# Revit family: QF_BPRO_CE 66-54_574906
name_source: partatom
category: Sonderausstattung
revit_build: Autodesk Revit 2018 (Build: 20190510_1515(x64)
units: mm (PartAtom-declared; Revit-internal decimal feet)

## family parameters
Arbeitsebenenbasiert = Nein
Beim Laden mit Abzugskörper schneiden = Nein
Bemaßung runder Anschluss = Durchmesser verwenden
Gemeinsam genutzt = Nein
Immer vertikal = Ja
Raumberechnungspunkt = Ja
Teiletyp = Normal

## types (1)
- CE 66-54
    Abdeckhaube Höhe = 167 mm  [stored 0.5479 ft]
    Abdeckhaube Länge = 710 mm
    Abdeckhaube Tiefe = 590 mm  [stored 1.9357 ft]
    Artikel Nummer = 574906
    Beschreibung = Korbspender, geschlossene Ausführung;
Korbmaße 650 x 530 mm;
Kapazität 6 Körbe à 115 mm oder 9 Körbe à 75 mm
    Beschreibung durch Hersteller analog Leistungsverzeichniskurztext = Abmessungen

Länge:					  885 mm
Breite:					  700 mm
Höhe:					  911 mm
Höhe (mit Option Abdeckhaube):		1067 mm
Arbeitshöhe:					  900 mm


Ausführung

Aufbau
Der Korbspender besteht komplett aus CNS 18/10. Die Oberfläche ist mikroliert. 
Der Korpus ist einwandig und kompakt in geschlossener Ausführung aufgebaut. Dadurch sind die Körbe vor Verschmutzung geschützt. 
Die Körbe werden auf eine Plattform aufgesetzt. Der Aufbau des Gerätes schützt vor dem Verrutschen der Körbe innerhalb des Spenders.
Durch Ein- bzw. Aushängen der Zugfedern kann die Federspannung entsprechend dem Stapelgut reguliert werden, um eine gleichbleibende Ausgabehöhe zu gewährleisten.
Bedienseitig ist ein CNS-Sicherheits-Schiebegriff mit seitlichen Stoßschutzelementen aus Kunststoff (Polyamid) angebracht.
Fahrbar ist der Spender mittels rostfreien Kunststoffrollen (4 Lenkrollen, 2 davon mit Feststeller mit 125 mm ø). Massive Stoßecken aus Kunststoff (Polyamid) an allen vier Ecken schützen vor Beschädigung.


Zubehör/ Optionen

•	Körbe aus Stahldraht, Kunststoff beschichtet
650 x 530 x 75 mm oder 650 x 530 x 115 mm
•	Körbe aus Edelstahl, rostfrei
650 x 530 x 75 mm oder 650 x 530 x 115 mm
•	Abdeckhaube (710 x 590 mm), Polycarbonat
Stapelhöhe mit Abdeckhaube:	680 mm
Stapelhöhe ohne Abdeckhaube:	540 mm
•	Weitere Zubehöre und Rollenausführungen siehe Gesamt-Preisliste



Technische Daten

Werkstoff:		CNS 18/10
Gewicht:		48 kg 
Plattform:		660 x 540 mm
Kapazität:		6 Körbe mit Höhe 115 mm,
		9 Körbe mit Höhe 75 mm


Besonderheit

•	Veränderung der Federspannung möglich
•	gemäß DIN 18665, Teil 6


Fabrikat

Hersteller:			B.PRO
Modell:				CE 66/ 54
Best.Nr.			574 906
    Beschreibung durch Hersteller analog Leistungsverzeichnislangtext = Abmessungen

Länge:					  885 mm
Breite:					  700 mm
Höhe:					  911 mm
Höhe (mit Option Abdeckhaube):		1067 mm
Arbeitshöhe:					  900 mm


Ausführung

Aufbau
Der Korbspender besteht komplett aus CNS 18/10. Die Oberfläche ist mikroliert. 
Der Korpus ist einwandig und kompakt in geschlossener Ausführung aufgebaut. Dadurch sind die Körbe vor Verschmutzung geschützt. 
Die Körbe werden auf eine Plattform aufgesetzt. Der Aufbau des Gerätes schützt vor dem Verrutschen der Körbe innerhalb des Spenders.
Durch Ein- bzw. Aushängen der Zugfedern kann die Federspannung entsprechend dem Stapelgut reguliert werden, um eine gleichbleibende Ausgabehöhe zu gewährleisten.
Bedienseitig ist ein CNS-Sicherheits-Schiebegriff mit seitlichen Stoßschutzelementen aus Kunststoff (Polyamid) angebracht.
Fahrbar ist der Spender mittels rostfreien Kunststoffrollen (4 Lenkrollen, 2 davon mit Feststeller mit 125 mm ø). Massive Stoßecken aus Kunststoff (Polyamid) an allen vier Ecken schützen vor Beschädigung.


Zubehör/ Optionen

•	Körbe aus Stahldraht, Kunststoff beschichtet
650 x 530 x 75 mm oder 650 x 530 x 115 mm
•	Körbe aus Edelstahl, rostfrei
650 x 530 x 75 mm oder 650 x 530 x 115 mm
•	Abdeckhaube (710 x 590 mm), Polycarbonat
Stapelhöhe mit Abdeckhaube:	680 mm
Stapelhöhe ohne Abdeckhaube:	540 mm
•	Weitere Zubehöre und Rollenausführungen siehe Gesamt-Preisliste



Technische Daten

Werkstoff:		CNS 18/10
Gewicht:		48 kg 
Plattform:		660 x 540 mm
Kapazität:		6 Körbe mit Höhe 115 mm,
		9 Körbe mit Höhe 75 mm


Besonderheit

•	Veränderung der Federspannung möglich
•	gemäß DIN 18665, Teil 6


Fabrikat

Hersteller:			B.PRO
Modell:				CE 66/ 54
Best.Nr.			574 906
    Gerätegewicht Netto = 48.00 kg
    Großküchengerätezuordnung = Ja
    Hersteller = B.PRO GmbH
    Höhe Korpus = 900 mm  [stored 2.95276 ft]
    Internetadresse Gerätehersteller = https://www.bpro-solutions.com
    Internetadresse für Ersatzteilliste = https://www.bpro-solutions.com
    Kosten = 1512.4 $
    Länge Gerätebreite = 885 mm  [stored 2.90354 ft]
    Länge Korpus = 780 mm  [stored 2.55906 ft]
    Material = QF_Metal-Stainless-Steel_general
    Material_Stoßschutz = QF_Rubber-Black-Matt
    Modell = CE 66-54
    Plattform Länge = 660 mm  [stored 2.16535 ft]
    Plattform Tiefe = 540 mm  [stored 1.77165 ft]
    Schacht Tiefe = 600 mm
    Sockelhöhe = 161 mm  [stored 0.528215 ft]
    Tiefe = 700 mm  [stored 2.29659 ft]
    Tiefe Korpus = 630 mm  [stored 2.06693 ft]
    Typenkommentare = Korbspender, geschlossene Ausführung
    URL = https://www.bpro-solutions.com
    Warnhinweise = Ausführliche Gefahrenhinweise entnehmen Sie der Betriebsanleitung.
    Zubehör = Nein

note: [stored X ft] marks values corroborated as IEEE doubles in the binary element streams (Revit-internal decimal feet)
